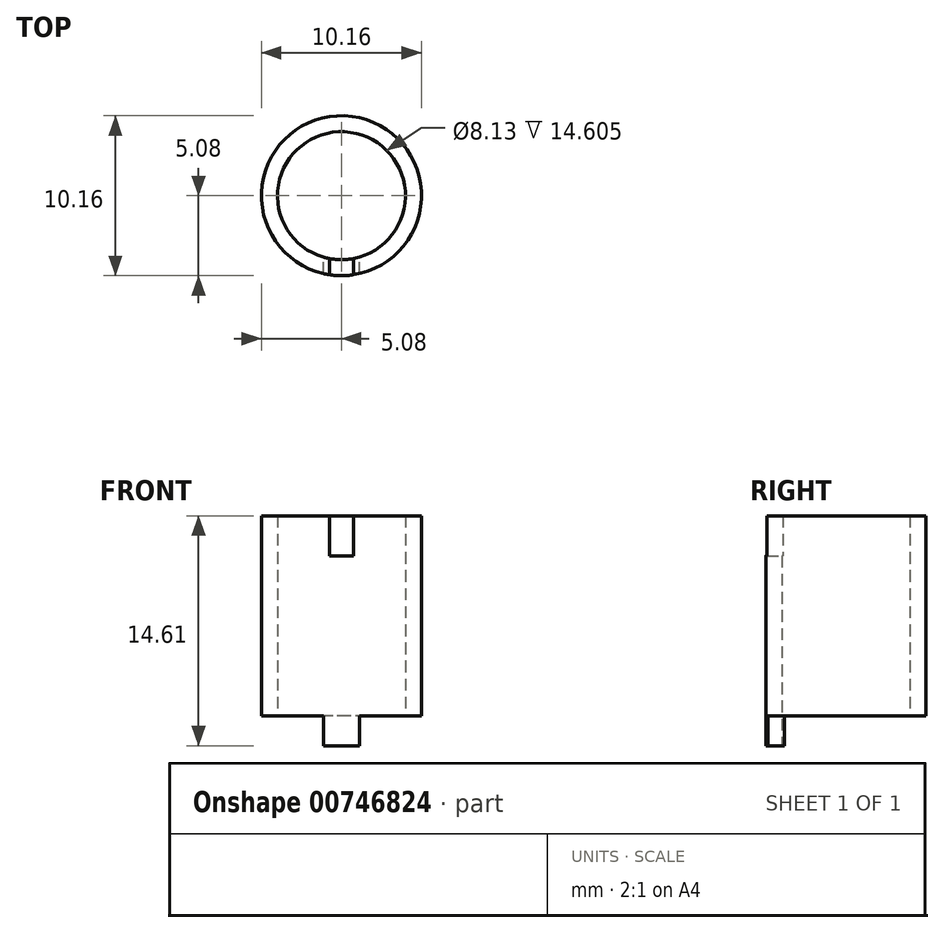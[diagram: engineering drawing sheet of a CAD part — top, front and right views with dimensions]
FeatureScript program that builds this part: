
annotation { "Feature Type Name" : "Feature", "Feature Type Description" : "" }
export const myFeature = defineFeature(function(context is Context, id is Id, definition is map)
    precondition{}
    {
        {
            var Q0;
            Q0=qCreatedBy(makeId("Top.planeOp"),FACE);
            var sketch = newSketch(context, id + "F0", { "sketchPlane" : qUnion([Q0])});
            skCircle(sketch, "E0", {"center": v(0, 0) * mm, "radius": 4.06 * mm});
            skCircle(sketch, "E1", {"center": v(0, 0) * mm, "radius": 5.08 * mm});
            skSolve(sketch);
        }
        {
            var Q0;
            Q0=makeQuery(id+"F0.imprint","IMPRINT",FACE,{"disambiguationData":[TD([[makeQuery(id+"F0.imprint","IMPRINT",EDGE,{"derivedFrom":sQuery(id+"F0.wireOp",EDGE,"E0")}),-1.0]])]});
            extrude(context, id + "F1", {"entities" : qUnion([Q0]), "depth" : 12.7 * mm, "offsetDistance" : 25.4 * mm});
        }
        {
            var Q0;
            Q0=qCreatedBy(makeId("Front.planeOp"),FACE);
            var sketch = newSketch(context, id + "F2", { "sketchPlane" : qUnion([Q0])});
            skLineSegment(sketch, "E2", {"start": v(-0.76, 12.7) * mm, "end": v(-0.76, 10.16) * mm});
            skLineSegment(sketch, "E3", {"start": v(-0.76, 10.16) * mm, "end": v(0.76, 10.16) * mm});
            skLineSegment(sketch, "E4", {"start": v(0.76, 10.16) * mm, "end": v(0.76, 12.7) * mm});
            skLineSegment(sketch, "E5", {"start": v(0.76, 12.7) * mm, "end": v(-0.76, 12.7) * mm});
            skPoint(sketch, "E6", {"position": v(0, 10.16) * mm});
            skSolve(sketch);
        }
        {
            var Q0;
            Q0=makeQuery(id+"F2.imprint","IMPRINT",FACE,{"disambiguationData":[TD([[makeQuery(id+"F2.imprint","IMPRINT",EDGE,{"derivedFrom":sQuery(id+"F2.wireOp",EDGE,"E2")}),1.0]])]});
            extrude(context, id + "F3", {"entities" : qUnion([Q0]), "operationType" : NewBodyOperationType.REMOVE, "depth" : 25.4 * mm, "offsetDistance" : 25.4 * mm});
        }
        {
            var Q0;
            Q0=qCreatedBy(makeId("Front.planeOp"),FACE);
            var sketch = newSketch(context, id + "F4", { "sketchPlane" : qUnion([Q0])});
            skLineSegment(sketch, "E7", {"start": v(-1.14, 0) * mm, "end": v(-1.14, -1.9) * mm});
            skLineSegment(sketch, "E8", {"start": v(-1.14, -1.9) * mm, "end": v(1.14, -1.9) * mm});
            skLineSegment(sketch, "E9", {"start": v(1.14, -1.9) * mm, "end": v(1.14, 0) * mm});
            skLineSegment(sketch, "E10", {"start": v(1.14, 0) * mm, "end": v(-1.14, 0) * mm});
            skSolve(sketch);
        }
        {
            var Q0;
            Q0=makeQuery(id+"F4.imprint","IMPRINT",FACE,{"disambiguationData":[TD([[makeQuery(id+"F4.imprint","IMPRINT",EDGE,{"derivedFrom":sQuery(id+"F4.wireOp",EDGE,"E7")}),1.0]])]});
            var Q1;
            Q1=makeQuery(id+"F1.opExtrude","SWEPT_FACE",FACE,{"disambiguationData":[OSD([sQuery(id+"F0.wireOp",EDGE,"E1")])]});
            extrude(context, id + "F5", {"entities" : qUnion([Q0]), "operationType" : NewBodyOperationType.ADD, "endBound" : BoundingType.UP_TO_SURFACE, "depth" : 25.4 * mm, "endBoundEntityFace" : qUnion([Q1]), "offsetDistance" : 25.4 * mm});
        }
        {
            var Q0;
            Q0 = qSketchRegion(id + "F4", true);
            var Q1;
            Q1=makeQuery(id+"F1.opExtrude","SWEPT_FACE",FACE,{"disambiguationData":[OSD([sQuery(id+"F0.wireOp",EDGE,"E0")])]});
            extrude(context, id + "F6", {"entities" : qUnion([Q0]), "operationType" : NewBodyOperationType.REMOVE, "endBound" : BoundingType.UP_TO_SURFACE, "depth" : 25.4 * mm, "endBoundEntityFace" : qUnion([Q1]), "offsetDistance" : 25.4 * mm});
        }
    });
